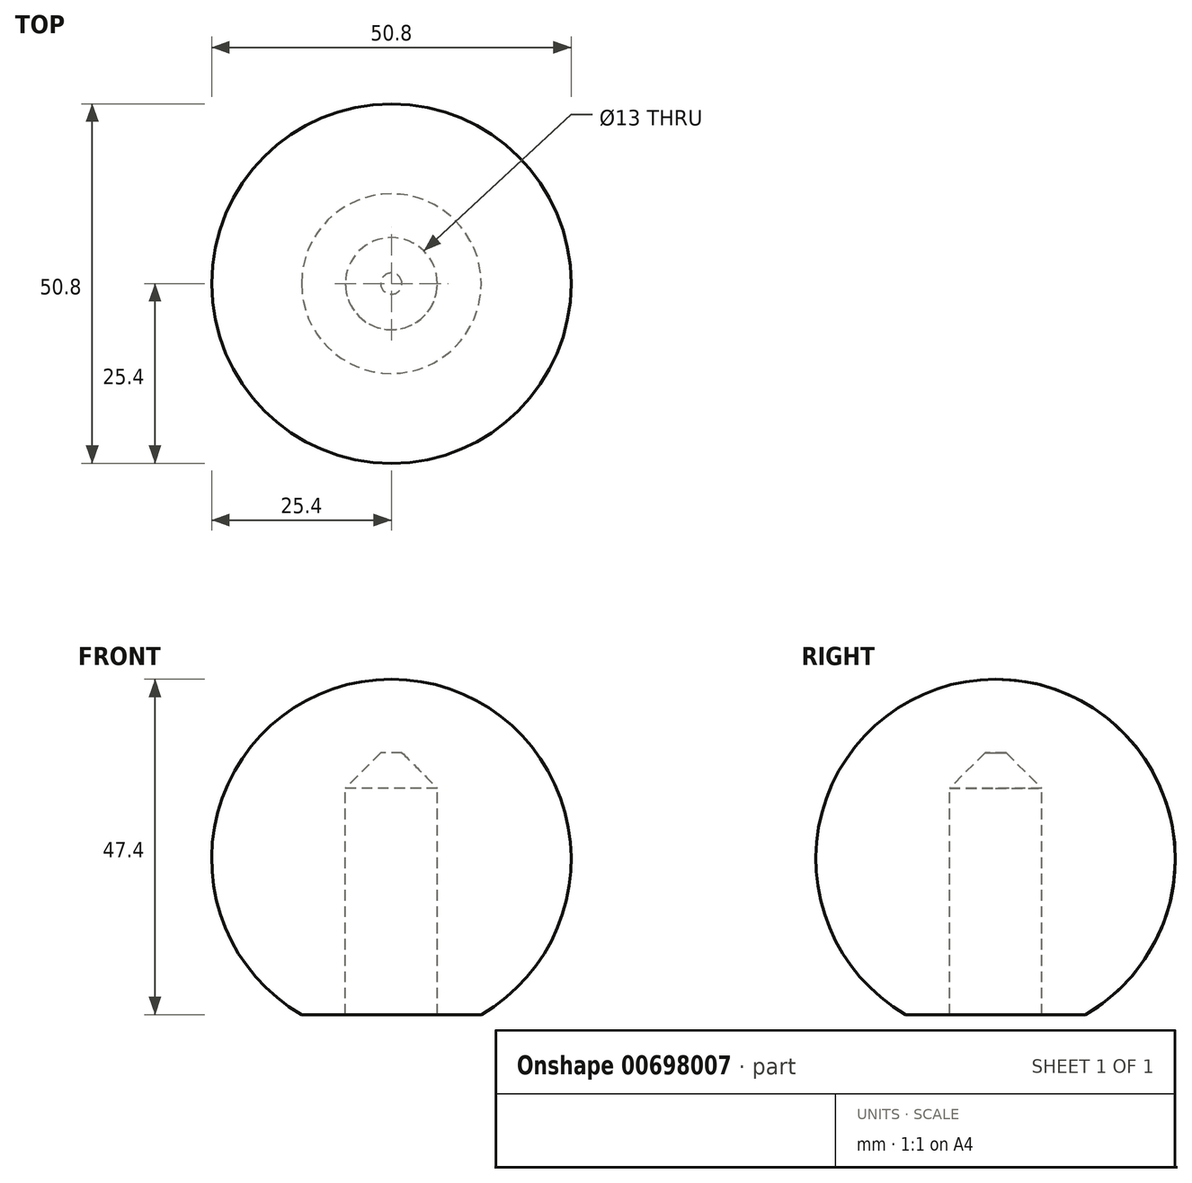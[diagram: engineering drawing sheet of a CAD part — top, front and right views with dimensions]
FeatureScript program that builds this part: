
annotation { "Feature Type Name" : "Feature", "Feature Type Description" : "" }
export const myFeature = defineFeature(function(context is Context, id is Id, definition is map)
    precondition{}
    {
        {
            var Q0;
            Q0=qCreatedBy(makeId("Right.planeOp"),FACE);
            var sketch = newSketch(context, id + "F0", { "sketchPlane" : qUnion([Q0])});
            skArc(sketch, "E0", {"start": v(0, 25.4) * mm, "mid": v(-25.4, 0) * mm, "end": v(0, -25.4) * mm});
            skLineSegment(sketch, "E1", {"start": v(0, 25.4) * mm, "end": v(0, -25.4) * mm});
            skSolve(sketch);
        }
        {
            var Q0;
            Q0=makeQuery(id+"F0.imprint","IMPRINT",FACE,{"disambiguationData":[TD([[makeQuery(id+"F0.imprint","IMPRINT",EDGE,{"derivedFrom":sQuery(id+"F0.wireOp",EDGE,"E0")}),1.0]])]});
            var Q1;
            Q1=sQuery(id+"F0.wireOp",EDGE,"E1");
            revolve(context, id + "F1", {"entities" : qUnion([Q0]), "axis" : qUnion([Q1]), "revolveType" : RevolveType.FULL});
        }
        {
            var Q0;
            Q0=qCreatedBy(makeId("Top.planeOp"),FACE);
            var sketch = newSketch(context, id + "F2", { "sketchPlane" : qUnion([Q0])});
            skCircle(sketch, "E2", {"center": v(0, 0) * mm, "radius": 6.5 * mm});
            skSolve(sketch);
        }
        {
            var Q0;
            Q0 = qSketchRegion(id + "F2", true);
            extrude(context, id + "F3", {"entities" : qUnion([Q0]), "operationType" : NewBodyOperationType.REMOVE, "oppositeDirection" : true, "depth" : 30 * mm, "offsetDistance" : 25 * mm});
        }
        {
            var Q0;
            Q0=qCreatedBy(makeId("Front.planeOp"),FACE);
            var sketch = newSketch(context, id + "F4", { "sketchPlane" : qUnion([Q0])});
            skLineSegment(sketch, "E3.bottom", {"start": v(-41.79, -22) * mm, "end": v(65.7, -22) * mm});
            skLineSegment(sketch, "E3.top", {"start": v(-41.79, -71.9) * mm, "end": v(65.7, -71.9) * mm});
            skLineSegment(sketch, "E3.left", {"start": v(-41.79, -22) * mm, "end": v(-41.79, -71.9) * mm});
            skLineSegment(sketch, "E3.right", {"start": v(65.7, -22) * mm, "end": v(65.7, -71.9) * mm});
            skSolve(sketch);
        }
        {
            var Q0;
            Q0=makeQuery(id+"F4.imprint","IMPRINT",FACE,{"disambiguationData":[TD([[makeQuery(id+"F4.imprint","IMPRINT",EDGE,{"derivedFrom":sQuery(id+"F4.wireOp",EDGE,"E3.bottom")}),-1.0]])]});
            extrude(context, id + "F5", {"entities" : qUnion([Q0]), "operationType" : NewBodyOperationType.REMOVE, "endBound" : BoundingType.SYMMETRIC, "oppositeDirection" : true, "depth" : 30 * mm, "offsetDistance" : 25 * mm});
        }
        {
            var Q0;
            Q0=makeQuery(id+"F3.boolean.opBoolean","COPY",FACE,{"derivedFrom":makeQuery(id+"F3.opExtrude","CAP_FACE",FACE,{"disambiguationData":[OSD([sQuery(id+"F2.wireOp",EDGE,"E2")])],"isStart":true})});
            extrude(context, id + "F6", {"entities" : qUnion([Q0]), "operationType" : NewBodyOperationType.REMOVE, "oppositeDirection" : true, "depth" : 15 * mm, "offsetDistance" : 25 * mm});
        }
        {
            var Q0;
            Q0=makeQuery(id+"F6.boolean.opBoolean","COPY",EDGE,{"derivedFrom":makeQuery(id+"F6.opExtrude","CAP_EDGE",EDGE,{"disambiguationData":[OSD([sQuery(id+"F2.wireOp",EDGE,"E2")])],"isStart":false})});
            chamfer(context, id + "F7", {"entities" : qUnion([Q0]), "width" : 5 * mm, "tangentPropagation" : true});
        }
    });
